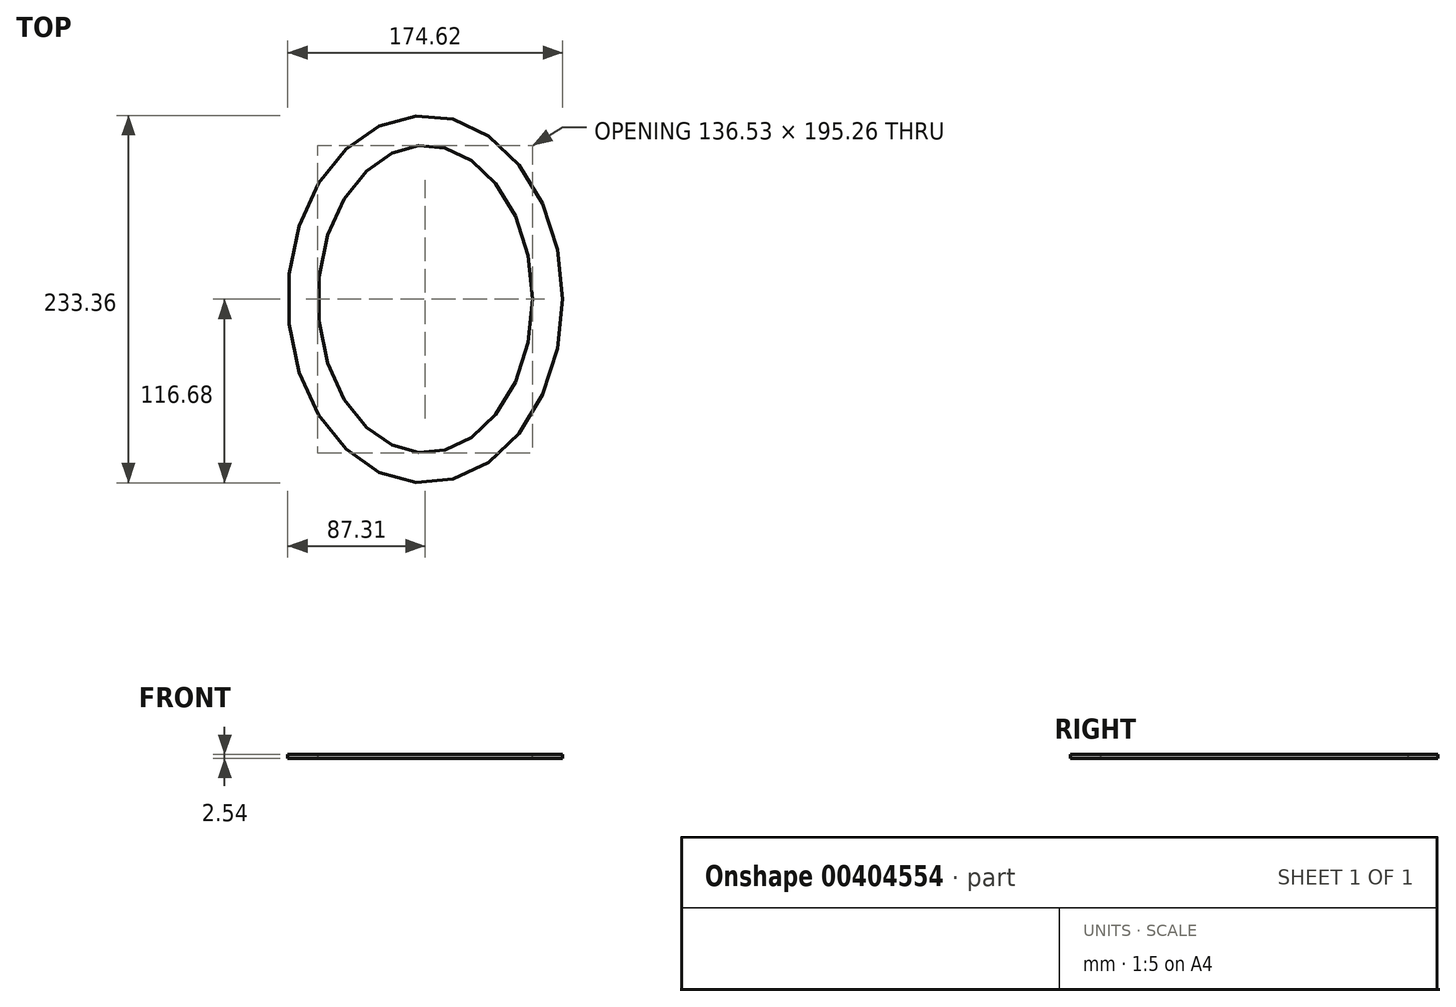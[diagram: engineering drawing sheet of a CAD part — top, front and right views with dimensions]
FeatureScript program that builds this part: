
annotation { "Feature Type Name" : "Feature", "Feature Type Description" : "" }
export const myFeature = defineFeature(function(context is Context, id is Id, definition is map)
    precondition{}
    {
        {
            var Q0;
            Q0=qCreatedBy(makeId("Top.planeOp"),FACE);
            var sketch = newSketch(context, id + "F0", { "sketchPlane" : qUnion([Q0])});
            skEllipse(sketch, "E0", {"center": v(0, 0) * mm, "majorRadius": 116.68 * mm, "minorRadius": 87.31 * mm, "majorAxis": v(0, 1)});
            skSolve(sketch);
        }
        {
            var Q0;
            Q0=qCreatedBy(makeId("Front.planeOp"),FACE);
            var sketch = newSketch(context, id + "F1", { "sketchPlane" : qUnion([Q0])});
            skLineSegment(sketch, "E1.bottom", {"start": v(87.31, 0) * mm, "end": v(68.26, 0) * mm});
            skLineSegment(sketch, "E1.top", {"start": v(87.31, 2.54) * mm, "end": v(68.26, 2.54) * mm});
            skLineSegment(sketch, "E1.left", {"start": v(87.31, 0) * mm, "end": v(87.31, 2.54) * mm});
            skLineSegment(sketch, "E1.right", {"start": v(68.26, 0) * mm, "end": v(68.26, 2.54) * mm});
            skLineSegment(sketch, "E2", {"start": v(0, 0) * mm, "end": v(0, 25.32) * mm, "construction": true});
            skSolve(sketch);
        }
        {
            var Q0;
            Q0=makeQuery(id+"F1.imprint","IMPRINT",FACE,{"disambiguationData":[TD([[makeQuery(id+"F1.imprint","IMPRINT",EDGE,{"derivedFrom":sQuery(id+"F1.wireOp",EDGE,"E1.bottom")}),-1.0]])]});
            var Q1;
            Q1=sQuery(id+"F0.wireOp",EDGE,"E0");
            sweep(context, id + "F2", {"profiles" : qUnion([Q0]), "path" : qUnion([Q1])});
        }
    });
